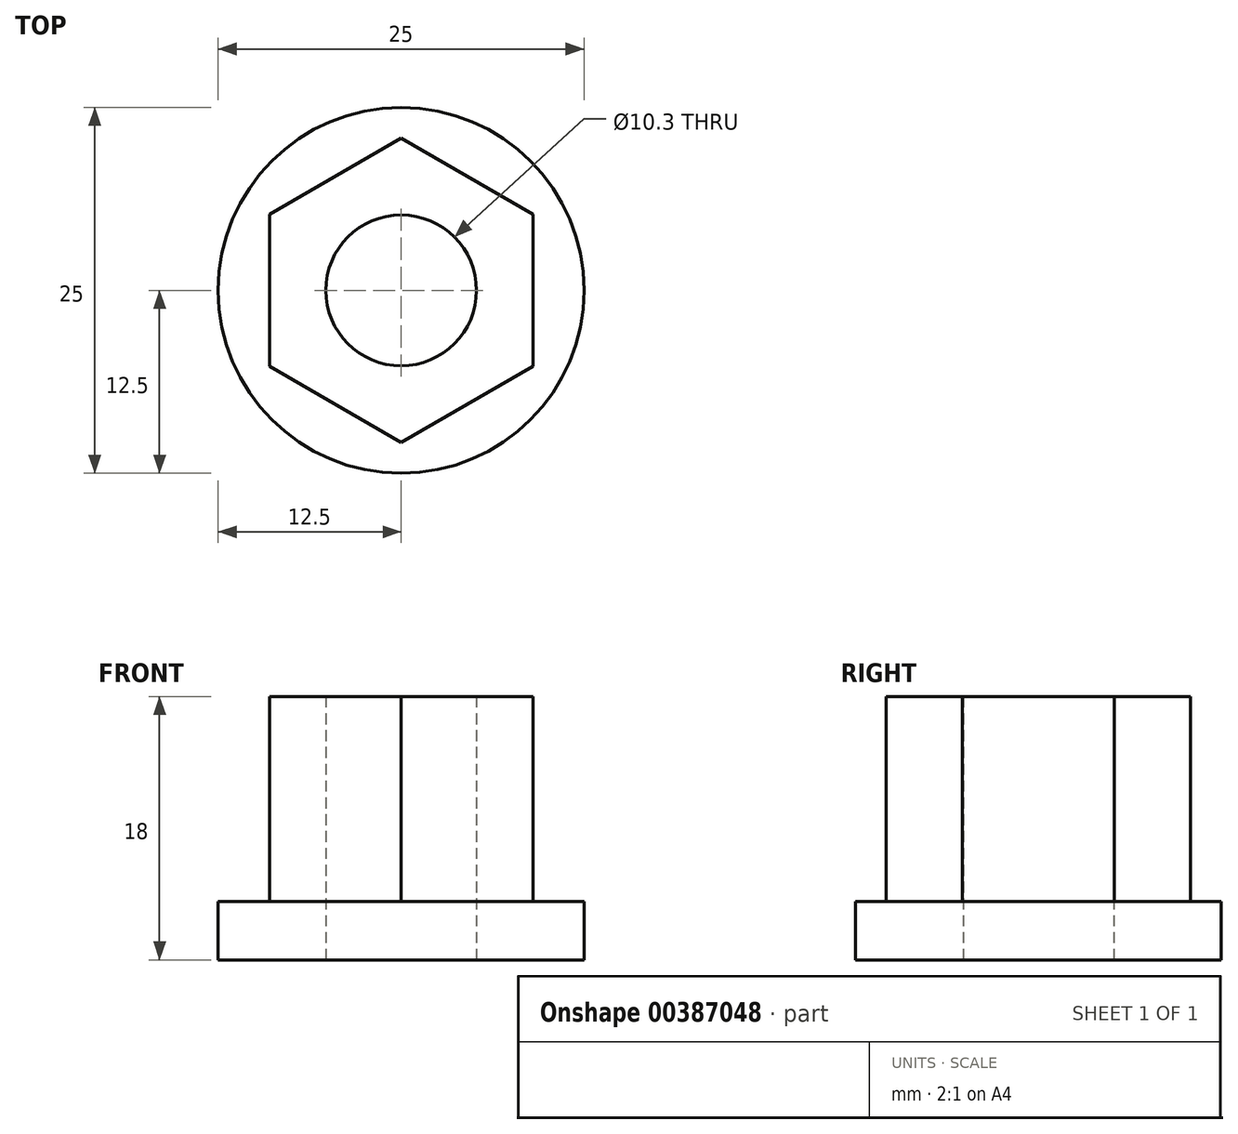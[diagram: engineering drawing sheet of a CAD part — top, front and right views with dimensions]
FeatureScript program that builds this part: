
annotation { "Feature Type Name" : "Feature", "Feature Type Description" : "" }
export const myFeature = defineFeature(function(context is Context, id is Id, definition is map)
    precondition{}
    {
        {
            var Q0;
            Q0=qCreatedBy(makeId("Top.planeOp"),FACE);
            var sketch = newSketch(context, id + "F0", { "sketchPlane" : qUnion([Q0])});
            skCircle(sketch, "E0", {"center": v(0, 0) * mm, "radius": 12.5 * mm});
            skSolve(sketch);
        }
        {
            var Q0;
            Q0=makeQuery(id+"F0.imprint","IMPRINT",FACE,{"disambiguationData":[TD([[makeQuery(id+"F0.imprint","IMPRINT",EDGE,{"derivedFrom":sQuery(id+"F0.wireOp",EDGE,"E0")}),1.0]])]});
            extrude(context, id + "F1", {"entities" : qUnion([Q0]), "oppositeDirection" : true, "depth" : 4 * mm});
        }
        {
            var Q0;
            Q0=makeQuery(id+"F1.opExtrude","CAP_FACE",FACE,{"disambiguationData":[OSD([sQuery(id+"F0.wireOp",EDGE,"E0")])],"isStart":true});
            var sketch = newSketch(context, id + "F2", { "sketchPlane" : qUnion([Q0])});
            skCircle(sketch, "E1.cCircle", {"center": v(0, 0) * mm, "radius": 9 * mm, "construction": true});
            skLineSegment(sketch, "E1.0", {"start": v(9, 5.2) * mm, "end": v(9, -5.2) * mm});
            skLineSegment(sketch, "E1.1", {"start": v(9, -5.2) * mm, "end": v(0, -10.4) * mm});
            skLineSegment(sketch, "E1.2", {"start": v(0, -10.4) * mm, "end": v(-9, -5.2) * mm});
            skLineSegment(sketch, "E1.3", {"start": v(-9, -5.2) * mm, "end": v(-9, 5.2) * mm});
            skLineSegment(sketch, "E1.4", {"start": v(-9, 5.2) * mm, "end": v(0, 10.4) * mm});
            skLineSegment(sketch, "E1.5", {"start": v(0, 10.4) * mm, "end": v(9, 5.2) * mm});
            skPoint(sketch, "E1.0.midPoint", {"position": v(9, 0) * mm});
            skSolve(sketch);
        }
        {
            var Q0;
            Q0=makeQuery(id+"F2.imprint","IMPRINT",FACE,{"disambiguationData":[TD([[makeQuery(id+"F2.imprint","IMPRINT",EDGE,{"derivedFrom":sQuery(id+"F2.wireOp",EDGE,"E1.0")}),-1.0]])]});
            extrude(context, id + "F3", {"entities" : qUnion([Q0]), "operationType" : NewBodyOperationType.ADD, "depth" : 14 * mm});
        }
        {
            var Q0;
            Q0=makeQuery(id+"F1.opExtrude","CAP_FACE",FACE,{"disambiguationData":[OSD([sQuery(id+"F0.wireOp",EDGE,"E0")])],"isStart":false});
            var sketch = newSketch(context, id + "F4", { "sketchPlane" : qUnion([Q0])});
            skPoint(sketch, "E2", {"position": v(0, 0) * mm});
            skSolve(sketch);
        }
        {
            var Q0;
            Q0=sQuery(id+"F4.wireOp",VERTEX,"E2");
            var Q1;
            Q1=makeQuery(id+"F1.opExtrude","SWEPT_BODY",BODY,{"disambiguationData":[OSD([sQuery(id+"F0.wireOp",EDGE,"E0")])]});
            hole(context, id + "F5", {"style" : HoleStyle.SIMPLE, "endStyle" : HoleEndStyle.THROUGH, "standardTappedOrClearance" : lookupTablePath({ "standard" : "ISO", "engagement" : "75%", "pitch" : "1.75 mm", "size" : "M12", "type" : "Tapped" }), "standardBlindInLast" : lookupTablePath({ "standard" : "ISO", "engagement" : "75%", "pitch" : "1.75 mm", "size" : "M12", "type" : "Tapped" }), "holeDiameter" : 10.3 * mm, "showTappedDepth" : true, "isTappedThrough" : true, "tappedDepth" : 12 * mm, "tapClearance" : 3, "startFromSketch" : true, "locations" : qUnion([Q0]), "scope" : qUnion([Q1]), "majorDiameter" : 12 * mm});
        }
    });
